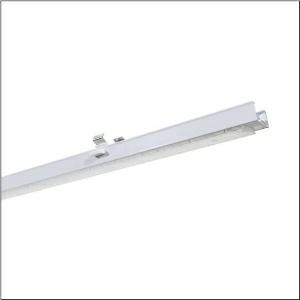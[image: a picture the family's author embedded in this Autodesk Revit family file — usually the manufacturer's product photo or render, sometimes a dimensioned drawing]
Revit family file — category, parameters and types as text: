
# Revit family: trunking_flex_31_51re18mb48b
name_source: partatom
category: Lighting Fixtures
units: mm (PartAtom-declared; Revit-internal decimal feet)

## family parameters
Cut with Voids When Loaded = No
Host = Face
Light Source = No
Part Type = Normal
Room Calculation Point = No
Round Connector Dimension = Use Diameter
Shared = No

## types (1)
- --- (1 x LED, 8000 lm, 50 W, 4000K)
    Apparent Load = 50 VA
    CIE Flux Codes = 71 89 97 97 100
    Color Rendering = 80
    Color Temperature = 4000K
    Default Elevation = 1800 mm
    Description = Trunking Flex 31, luminaire insert, of extruded aluminium section, coated, traffic white (RAL 9016), length: 1.472mm, width: 91mm, height: 53mm, LED rated luminous flux: 8.000lm, light colour: 840, control gear: ON/OFF Multilumen, with system connector: socket, mains connection: 220..240V, AC, 50/60Hz, rated input power: 50W, luminous flux adjustable on luminaire in four steps (4130/5610/6850/8000lm), connected load according to luminous flux setting (25/34/42/50W), primary light control with lens, of plastic, primary optical cover: cover, of PMMA, light emission: direct distribution, protection rating (complete): IP20, insulation class (complete): insulation class I (protective earthing), certification: CE, UKCA, impact resistance: IK02, permissible ambient temperature for indoor applications: -20..+40°C, packaging unit: 1 piece
    Height = 58 mm
    Lamp = 1 x LED
    Lamp Light Flux = 8000 lm
    Lamp Power = 50 W
    Lamp count = 1
    Length = 1472 mm
    Luminous efficacy = 160 lm/W
    Manufacturer = Siteco
    ModVariant = No
    Model = 51RE18MB48B
    Mounting Place = Ceiling
    Mounting Type = Pendant
    Number of Poles = 1
    OnlyDefault = Yes
    Power Factor = 1
    Product Name = Trunking Flex 31
    Product group = luminaire insert
    ProductGroupID = 902
    Protection Class = Protection class I
    Protection Degree = IP 20
    RLX_Detail_Level = 1
    RLX_Emergency_Light_Flux = 0 lm
    RLX_Emergency_Type = 0
    RLX_Emergency_Type_DB = No
    RlxData = <blob elided: 20365 chars, md5=4f429fe9>
    Socket = socket
    Standby Power = 0 W
    System Light Flux = 8000 lm
    System Power = 50 W
    Type Comments = factory setting: luminous flux: 100 % | (ON | ON) | 300 mA
    Type Image = l_1266702.jpg
    URL = http://relux.com
    VarID = @adj_059078
    Voltage = 0 V
    Weight = 0.00 kg
    Width = 65 mm

## geometry (parser evidence)
native form markers: Blend x4, Sweep x11
no freeform markers — native parametric forms only
